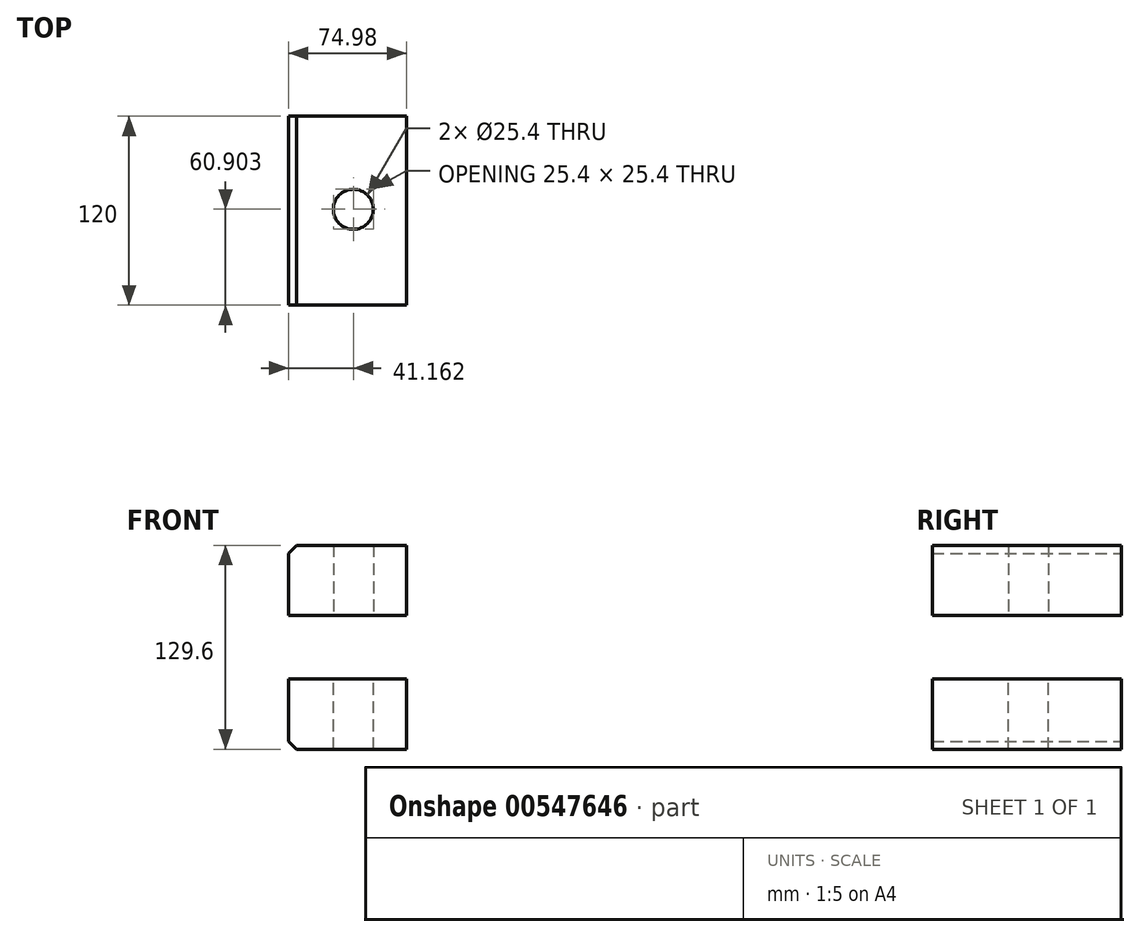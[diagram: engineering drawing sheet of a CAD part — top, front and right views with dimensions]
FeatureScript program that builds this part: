
annotation { "Feature Type Name" : "Feature", "Feature Type Description" : "" }
export const myFeature = defineFeature(function(context is Context, id is Id, definition is map)
    precondition{}
    {
        {
            var Q0;
            Q0=qCreatedBy(makeId("Front.planeOp"),FACE);
            var sketch = newSketch(context, id + "F0", { "sketchPlane" : qUnion([Q0])});
            skLineSegment(sketch, "E0.bottom", {"start": v(-74.98, 64.8) * mm, "end": v(0, 64.8) * mm});
            skLineSegment(sketch, "E0.top", {"start": v(-74.98, 20.25) * mm, "end": v(0, 20.25) * mm});
            skLineSegment(sketch, "E0.left", {"start": v(-74.98, 64.8) * mm, "end": v(-74.98, 20.25) * mm});
            skLineSegment(sketch, "E0.right", {"start": v(0, 64.8) * mm, "end": v(0, 20.25) * mm});
            skSolve(sketch);
        }
        {
            var Q0;
            Q0 = qSketchRegion(id + "F0", true);
            extrude(context, id + "F1", {"entities" : qUnion([Q0]), "depth" : 120 * mm, "offsetDistance" : 25.4 * mm});
        }
        {
            var Q0;
            Q0=makeQuery(id+"F1.opExtrude","SWEPT_EDGE",EDGE,{"disambiguationData":[OSD([sQuery(id+"F0.wireOp",EDGE,"E0.bottom"),sQuery(id+"F0.wireOp",EDGE,"E0.left")])]});
            chamfer(context, id + "F2", {"entities" : qUnion([Q0]), "width" : 5.08 * mm, "tangentPropagation" : true});
        }
        {
            var Q0;
            Q0=makeQuery(id+"F1.opExtrude","SWEPT_FACE",FACE,{"disambiguationData":[OSD([sQuery(id+"F0.wireOp",EDGE,"E0.top")])]});
            var sketch = newSketch(context, id + "F3", { "sketchPlane" : qUnion([Q0])});
            skPoint(sketch, "E1", {"position": v(-33.82, 59.1) * mm});
            skSolve(sketch);
        }
        {
            var Q0;
            Q0=sQuery(id+"F3.wireOp",VERTEX,"E1");
            var Q1;
            Q1=makeQuery(id+"F1.opExtrude","SWEPT_BODY",BODY,{"disambiguationData":[OSD([sQuery(id+"F0.wireOp",EDGE,"E0.bottom"),sQuery(id+"F0.wireOp",EDGE,"E0.top"),sQuery(id+"F0.wireOp",EDGE,"E0.left"),sQuery(id+"F0.wireOp",EDGE,"E0.right")])]});
            hole(context, id + "F4", {"style" : HoleStyle.SIMPLE, "endStyle" : HoleEndStyle.THROUGH, "holeDiameter" : 25.4 * mm, "isTappedThrough" : true, "tappedDepth" : 12.7 * mm, "tapClearance" : 3, "locations" : qUnion([Q0]), "scope" : qUnion([Q1])});
        }
        {
            var Q0;
            Q0=makeQuery(id+"F1.opExtrude","SWEPT_BODY",BODY,{"disambiguationData":[OSD([sQuery(id+"F0.wireOp",EDGE,"E0.bottom"),sQuery(id+"F0.wireOp",EDGE,"E0.top"),sQuery(id+"F0.wireOp",EDGE,"E0.left"),sQuery(id+"F0.wireOp",EDGE,"E0.right")])]});
            var Q1;
            Q1=qCreatedBy(makeId("Top.planeOp"),FACE);
            mirror(context, id + "F5", {"entities" : qUnion([Q0]), "mirrorPlane" : qUnion([Q1])});
        }
    });
